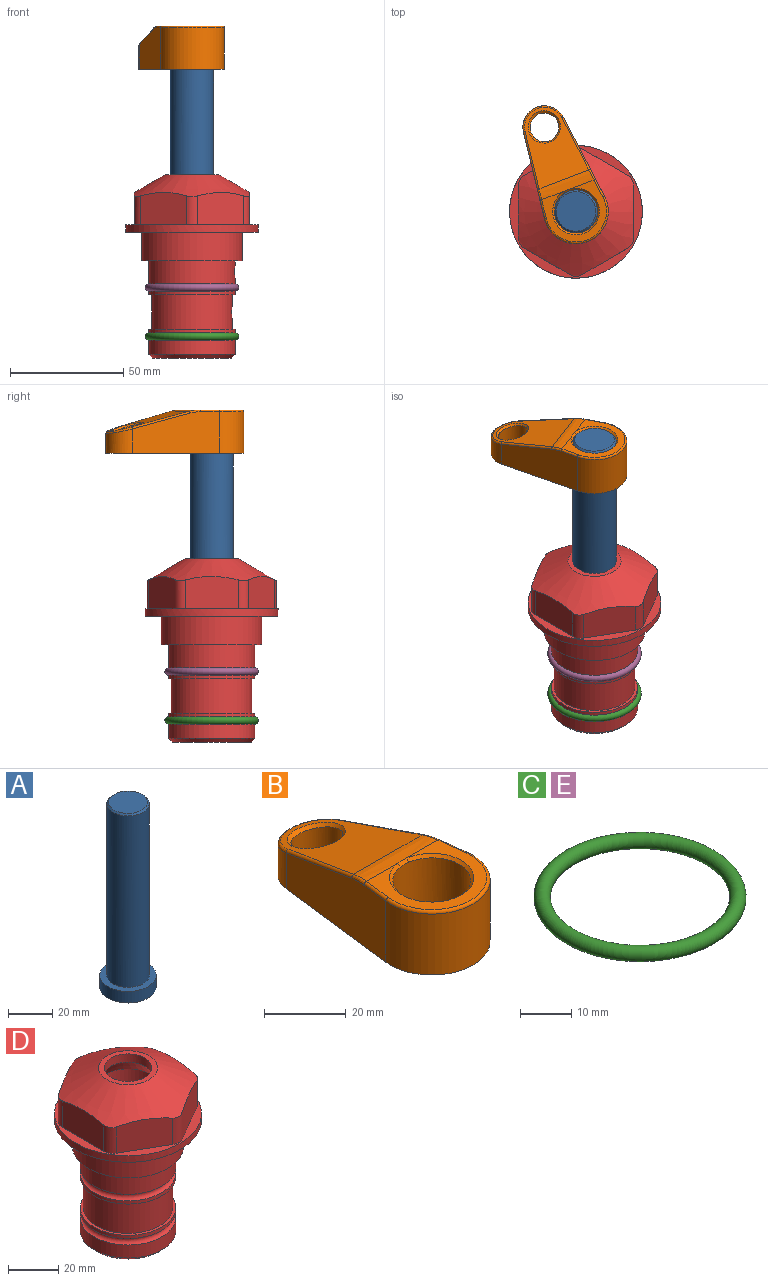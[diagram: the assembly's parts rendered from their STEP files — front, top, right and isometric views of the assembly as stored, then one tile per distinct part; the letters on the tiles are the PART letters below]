
ASSEMBLY  parts=5 mates=4
PART A: 6 faces, bbox 25.4x25.4x101.6 mm
  f0: plane 17.46x17.46mm, normal (0,0,1), area 239.5mm2, adj f5
  f1: plane 25.4x25.4mm, normal (0,0,-1), area 506.7mm2, adj f2
  f2: cylinder r=12.7mm len=25.4mm, axis (0,0,1), area 506.7mm2, adj f1,f3
  f3: plane 25.4x25.4mm, normal (0,0,1), area 221.7mm2, adj f2,f4
  f4: cylinder r=9.53mm len=94.46mm, axis (0,0,1), area 5653mm2, adj f3,f5
  f5: cone r=8.73mm half-angle=45deg, axis (0,0,-1), area 64.4mm2, adj f0,f4
PART B: 31 faces, bbox 31.7x65.5x19.8 mm
  f0: plane 39.12x18.26mm, normal (0.99,0.12,0), area 612.2mm2, adj f1,f4,f7,f11,f13,f15
  f1: cylinder r=9.53mm len=18.91mm, axis (0,0,-1), area 296.1mm2, adj f0,f2,f7,f17
  f2: plane 39.12x18.26mm, normal (-0.99,0.12,0), area 612.2mm2, adj f1,f4,f7,f12,f14,f16
  f3: cylinder r=6.35mm len=12.7mm, axis (0,0,-1), area 362.4mm2, adj f7,f18
  f4: cylinder r=14.29mm len=28.58mm, axis (0,0,-1), area 882.2mm2, adj f0,f2,f7,f10
  f5: cylinder r=9.53mm len=19.05mm, axis (0,0,-1), area 1092.6mm2, adj f7,f19,f20
  f6: plane 26.99x23.69mm, normal (0,0,1), area 216.2mm2, adj f9,f10,f11,f12,f19
  f7: plane 63.5x28.58mm, normal (0,0,-1), area 661.8mm2, adj f0,f1,f2,f3,f4,f5,f22,f23
  f8: plane 33.52x23.6mm, normal (0,0.26,0.97), area 486mm2, adj f9,f15,f16,f17,f18
  f9: cylinder r=19.05mm len=24.72mm, axis (1,0,0), area 120.4mm2, adj f6,f8,f13,f14,f20
  f10: torus R=13.49mm, axis (0,0,1), area 59mm2, adj f4,f6,f11,f12
  f11: cylinder r=0.79mm len=8.67mm, axis (0.12,-0.99,0), area 10.8mm2, adj f0,f6,f10,f13
  f12: cylinder r=0.79mm len=8.67mm, axis (0.12,0.99,0), area 10.8mm2, adj f2,f6,f10,f14
  f13: bspline ~4.95x1.42mm, area 6.1mm2, adj f0,f9,f11,f15
  f14: bspline ~4.95x1.42mm, area 6.1mm2, adj f2,f9,f12,f16
  f15: cylinder r=0.79mm len=25.95mm, axis (0.12,-0.96,0.26), area 32.9mm2, adj f0,f8,f13,f17
  f16: cylinder r=0.79mm len=25.95mm, axis (0.12,0.96,-0.26), area 32.9mm2, adj f2,f8,f14,f17
  f17: bspline ~18.91x8.38mm, area 30mm2, adj f1,f8,f15,f16
  f18: bspline ~14.29x14.29mm, area 48.3mm2, adj f3,f8
  f19: cone r=9.53mm half-angle=45deg, axis (0,0,1), area 66.5mm2, adj f5,f6,f20
  f20: bspline ~3.22x0.96mm, area 3.5mm2, adj f5,f9,f19
  f21: plane 2.75x2.72mm, normal (0,0,-1), area 2.9mm2, adj f23,f25,f28
  f22: plane 23.05x15.88mm, normal (-0.99,-0.12,0), area 323.6mm2, adj f7,f25,f26,f27,f28,f29
  f23: plane 23.05x15.88mm, normal (0.99,-0.12,0), area 323.6mm2, adj f7,f21,f25,f27,f28,f30
  f24: cylinder r=9.53mm len=10.69mm, axis (0,0,-1), area 114.7mm2, adj f7,f27,f29,f30
  f25: cylinder r=12.7mm len=20.59mm, axis (0,0,-1), area 381.1mm2, adj f7,f21,f22,f23,f26,f28
  f26: plane 2.75x2.72mm, normal (0,0,-1), area 2.9mm2, adj f22,f25,f28
  f27: plane 19.72x18.37mm, normal (0,-0.26,-0.97), area 291.8mm2, adj f22,f23,f24,f28,f29,f30
  f28: cylinder r=15.88mm len=19.92mm, axis (1,0,0), area 54.8mm2, adj f21,f22,f23,f25,f26,f27
  f29: cylinder r=1.59mm len=11mm, axis (0,0,-1), area 34.7mm2, adj f7,f22,f24,f27
  f30: cylinder r=1.59mm len=11mm, axis (0,0,-1), area 34.7mm2, adj f7,f23,f24,f27
PART C: 1 faces, bbox 44.7x44.7x3.2 mm
  f0: torus R=19.05mm, axis (0,0,1), area 1193.9mm2
PART D: 36 faces, bbox 58.7x58.7x81 mm
  f0: cylinder r=17.78mm len=35.56mm, axis (0,0,1), area 1670.8mm2, adj f23,f24,f31
  f1: cylinder r=19.05mm len=38.1mm, axis (0,0,1), area 1191.9mm2, adj f26,f27,f30
  f2: plane 58.66x58.66mm, normal (0,0,-1), area 1150.6mm2, adj f3,f28
  f3: cylinder r=29.33mm len=58.66mm, axis (0,0,-1), area 585.1mm2, adj f2,f4
  f4: plane 58.66x58.66mm, normal (0,0,1), area 475.9mm2, adj f3,f5,f6,f7,f8,f9,f10,f11
  f5: plane 20.32x14.34mm, normal (-0.5,0.87,0), area 324.4mm2, adj f4,f15,f16,f17
  f6: plane 20.32x14.34mm, normal (0.5,0.87,0), area 324.4mm2, adj f4,f14,f15,f17
  f7: plane 23.48x14.34mm, normal (1,0,0), area 324.4mm2, adj f4,f13,f14,f17
  f8: plane 20.32x14.34mm, normal (0.5,-0.87,0), area 324.4mm2, adj f4,f12,f13,f17
  f9: plane 20.32x14.34mm, normal (-0.5,-0.87,0), area 324.4mm2, adj f4,f11,f12,f17
  f10: plane 23.48x14.34mm, normal (-1,0,0), area 324.4mm2, adj f4,f11,f16,f17
  f11: cylinder r=5.08mm len=12.85mm, axis (0,0,-1), area 67.2mm2, adj f4,f9,f10,f17
  f12: cylinder r=5.08mm len=12.85mm, axis (0,0,-1), area 67.2mm2, adj f4,f8,f9,f17
  f13: cylinder r=5.08mm len=12.85mm, axis (0,0,-1), area 67.2mm2, adj f4,f7,f8,f17
  f14: cylinder r=5.08mm len=12.85mm, axis (0,0,-1), area 67.2mm2, adj f4,f6,f7,f17
  f15: cylinder r=5.08mm len=12.85mm, axis (0,0,-1), area 67.2mm2, adj f4,f5,f6,f17
  f16: cylinder r=5.08mm len=12.85mm, axis (0,0,-1), area 67.2mm2, adj f4,f5,f10,f17
  f17: cone r=11.73mm half-angle=60deg, axis (0,0,-1), area 2071.8mm2, adj f5,f6,f7,f8,f9,f10,f11,f12
  f18: plane 23.46x23.46mm, normal (0,0,1), area 147.4mm2, adj f17,f35
  f19: plane 34.93x34.93mm, normal (0,0,-1), area 958mm2, adj f29
  f20: cylinder r=19.05mm len=38.1mm, axis (0,0,1), area 760.1mm2, adj f21,f29
  f21: torus R=19.05mm, axis (0,0,1), area 565.3mm2, adj f20,f22
  f22: cylinder r=19.05mm len=38.1mm, axis (0,0,1), area 190mm2, adj f21,f23
  f23: plane 38.1x38.1mm, normal (0,0,1), area 146.9mm2, adj f0,f22
  f24: plane 38.1x38.1mm, normal (0,0,-1), area 146.9mm2, adj f0,f25
  f25: cylinder r=19.05mm len=38.1mm, axis (0,0,1), area 190mm2, adj f24,f26
  f26: torus R=19.05mm, axis (0,0,1), area 565.3mm2, adj f1,f25
  f27: plane 44.45x44.45mm, normal (0,0,-1), area 411.7mm2, adj f1,f28
  f28: cylinder r=22.23mm len=44.45mm, axis (0,0,1), area 1773.5mm2, adj f2,f27
  f29: cone r=19.05mm half-angle=45deg, axis (0,0,1), area 257.5mm2, adj f19,f20
  f30: cylinder r=3.17mm len=6.75mm, axis (-1,0,0), area 128mm2, adj f1,f33
  f31: cylinder r=3.17mm len=6.35mm, axis (-1,0,0), area 102.5mm2, adj f0,f33
  f32: plane 25.4x25.4mm, normal (0,0,1), area 506.7mm2, adj f33
  f33: cylinder r=12.7mm len=66.42mm, axis (0,0,-1), area 5236.2mm2, adj f30,f31,f32,f34
  f34: cone r=9.53mm half-angle=30deg, axis (0,0,-1), area 443.4mm2, adj f33,f35
  f35: cylinder r=9.53mm len=19.05mm, axis (0,0,-1), area 240.9mm2, adj f18,f34
PART E: same geometry as C
PLACE A rot(axis=(0,0,1),20.6deg) t=(0,0,27.55)mm
PLACE B rot(axis=(0,0,1),20.6deg) t=(0,0,27.55)mm
PLACE C t=(0,0,-21.59)mm
PLACE D at identity fixed
PLACE E at identity
MATE fastened B.f4 <-> A.f2  axis (0,0,1) through (0,0,91.05)mm
MATE fastened E.f0 <-> D.f0  axis (0,0,1) through (0,0,-24.51)mm
MATE fastened C.f0 <-> D.f0  axis (0,0,1) through (0,0,-46.1)mm
MATE cylindrical A.f2 <-> D.f0  axis (0,0,-1) through (0,0,-10.55)mm
